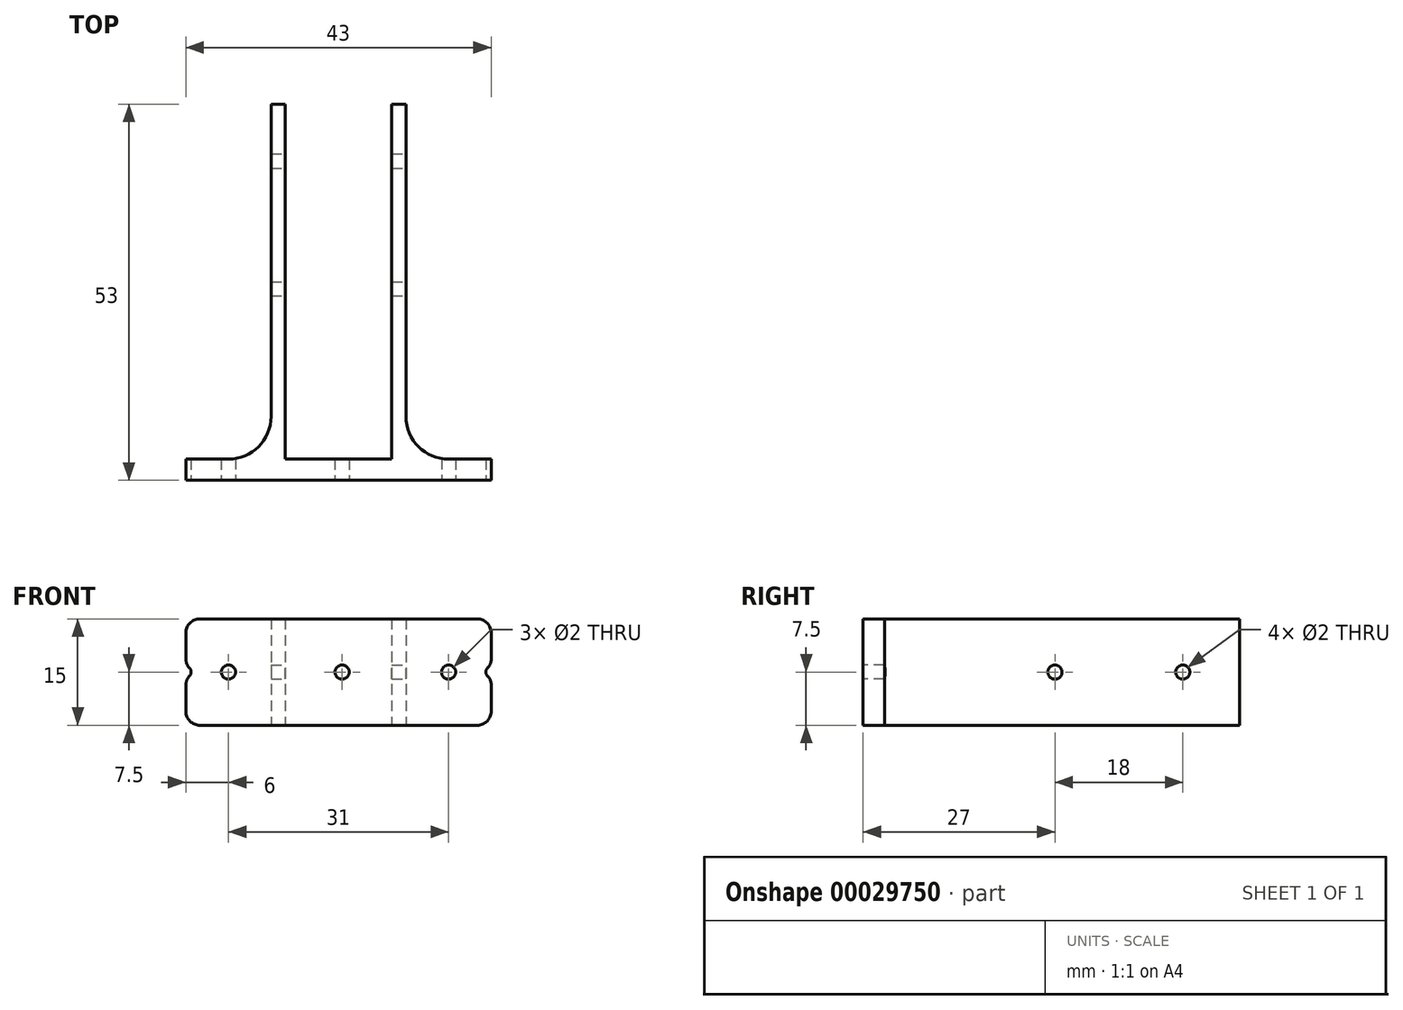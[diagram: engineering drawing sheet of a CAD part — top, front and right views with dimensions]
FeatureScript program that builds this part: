
annotation { "Feature Type Name" : "Feature", "Feature Type Description" : "" }
export const myFeature = defineFeature(function(context is Context, id is Id, definition is map)
    precondition{}
    {
        {
            var Q0;
            Q0=qCreatedBy(makeId("Top.planeOp"),FACE);
            var sketch = newSketch(context, id + "F0", { "sketchPlane" : qUnion([Q0])});
            skLineSegment(sketch, "E0.top", {"start": v(0, 53) * mm, "end": v(-2, 53) * mm});
            skLineSegment(sketch, "E0.left", {"start": v(0, 3) * mm, "end": v(0, 53) * mm});
            skLineSegment(sketch, "E0.right", {"start": v(-19, 3) * mm, "end": v(-19, 53) * mm});
            skLineSegment(sketch, "E1.top", {"start": v(-17, 3) * mm, "end": v(-2, 3) * mm});
            skLineSegment(sketch, "E1.left", {"start": v(-17, 53) * mm, "end": v(-17, 3) * mm});
            skLineSegment(sketch, "E1.right", {"start": v(-2, 53) * mm, "end": v(-2, 3) * mm});
            skLineSegment(sketch, "E2.trimOffspring", {"start": v(-17, 53) * mm, "end": v(-19, 53) * mm});
            skLineSegment(sketch, "E3", {"start": v(-19, 0) * mm, "end": v(0, 0) * mm});
            skLineSegment(sketch, "E4", {"start": v(-19, 0) * mm, "end": v(-31, 0) * mm});
            skLineSegment(sketch, "E5", {"start": v(-31, 0) * mm, "end": v(-31, 3) * mm});
            skLineSegment(sketch, "E6", {"start": v(-31, 3) * mm, "end": v(-19, 3) * mm});
            skLineSegment(sketch, "E7", {"start": v(0, 3) * mm, "end": v(12, 3) * mm});
            skLineSegment(sketch, "E8", {"start": v(12, 3) * mm, "end": v(12, 0) * mm});
            skLineSegment(sketch, "E9", {"start": v(12, 0) * mm, "end": v(0, 0) * mm});
            skSolve(sketch);
        }
        {
            var Q0;
            Q0=makeQuery(id+"F0.imprint","IMPRINT",FACE,{"disambiguationData":[TD([[makeQuery(id+"F0.imprint","IMPRINT",EDGE,{"derivedFrom":sQuery(id+"F0.wireOp",EDGE,"E0.top")}),1.0]])]});
            extrude(context, id + "F1", {"entities" : qUnion([Q0]), "depth" : 15 * mm});
        }
        {
            var Q0;
            Q0=makeQuery(id+"F1.opExtrude","SWEPT_FACE",FACE,{"disambiguationData":[OSD([sQuery(id+"F0.wireOp",EDGE,"E0.left")])]});
            var sketch = newSketch(context, id + "F2", { "sketchPlane" : qUnion([Q0])});
            skCircle(sketch, "E10", {"center": v(27, 7.5) * mm, "radius": 1 * mm});
            skCircle(sketch, "E11", {"center": v(45, 7.5) * mm, "radius": 1 * mm});
            skSolve(sketch);
        }
        {
            var Q0;
            Q0=qSketchRegion(id+"F2",true);
            extrude(context, id + "F3", {"entities" : qUnion([Q0]), "operationType" : NewBodyOperationType.REMOVE, "oppositeDirection" : true, "depth" : 25 * mm});
        }
        {
            var Q0;
            Q0=makeQuery(id+"F1.opExtrude","SWEPT_EDGE",EDGE,{"disambiguationData":[OSD([sQuery(id+"F0.wireOp",EDGE,"E0.left"),sQuery(id+"F0.wireOp",EDGE,"E7")])]});
            var Q1;
            Q1=makeQuery(id+"F1.opExtrude","SWEPT_EDGE",EDGE,{"disambiguationData":[OSD([sQuery(id+"F0.wireOp",EDGE,"E0.right"),sQuery(id+"F0.wireOp",EDGE,"E6")])]});
            fillet(context, id + "F4", {"entities" : qUnion([Q0, Q1]), "radius" : 6 * mm, "tangentPropagation" : true, "allowEdgeOverflow" : false});
        }
        {
            var Q0;
            Q0=makeQuery(id+"F1.opExtrude","SWEPT_FACE",FACE,{"disambiguationData":[OSD([sQuery(id+"F0.wireOp",EDGE,"E3"),sQuery(id+"F0.wireOp",EDGE,"E4"),sQuery(id+"F0.wireOp",EDGE,"E9")])]});
            var sketch = newSketch(context, id + "F5", { "sketchPlane" : qUnion([Q0])});
            skCircle(sketch, "E12", {"center": v(-9, 7.5) * mm, "radius": 1 * mm});
            skCircle(sketch, "E13", {"center": v(-25, 7.5) * mm, "radius": 1 * mm});
            skCircle(sketch, "E14", {"center": v(6, 7.5) * mm, "radius": 1 * mm});
            skLineSegment(sketch, "E15.0", {"start": v(12, 15) * mm, "end": v(12, 0) * mm});
            skCircle(sketch, "E16", {"center": v(-31, 7.5) * mm, "radius": 0.75 * mm});
            skCircle(sketch, "E17", {"center": v(12, 7.5) * mm, "radius": 0.75 * mm});
            skSolve(sketch);
        }
        {
            var Q0;
            Q0 = qSketchRegion(id + "F5", true);
            extrude(context, id + "F6", {"entities" : qUnion([Q0]), "operationType" : NewBodyOperationType.REMOVE, "oppositeDirection" : true, "depth" : 25 * mm});
        }
        {
            var Q0;
            Q0=makeQuery(id+"F6.boolean.opBoolean","INTERSECT",EDGE,{"disambiguationData":[OD(1.0)],"derivedFrom":[makeQuery(id+"F1.opExtrude","SWEPT_FACE",FACE,{"disambiguationData":[OSD([sQuery(id+"F0.wireOp",EDGE,"E5")])]}),makeQuery(id+"F6.opExtrude","SWEPT_FACE",FACE,{"disambiguationData":[OSD([sQuery(id+"F5.wireOp",EDGE,"E16")])]})]});
            var Q1;
            Q1=makeQuery(id+"F6.boolean.opBoolean","INTERSECT",EDGE,{"disambiguationData":[OD(0.0)],"derivedFrom":[makeQuery(id+"F1.opExtrude","SWEPT_FACE",FACE,{"disambiguationData":[OSD([sQuery(id+"F0.wireOp",EDGE,"E5")])]}),makeQuery(id+"F6.opExtrude","SWEPT_FACE",FACE,{"disambiguationData":[OSD([sQuery(id+"F5.wireOp",EDGE,"E16")])]})]});
            var Q2;
            Q2=makeQuery(id+"F6.boolean.opBoolean","INTERSECT",EDGE,{"disambiguationData":[OD(1.0)],"derivedFrom":[makeQuery(id+"F1.opExtrude","SWEPT_FACE",FACE,{"disambiguationData":[OSD([sQuery(id+"F0.wireOp",EDGE,"E8")])]}),makeQuery(id+"F6.opExtrude","SWEPT_FACE",FACE,{"disambiguationData":[OSD([sQuery(id+"F5.wireOp",EDGE,"E17")])]})]});
            var Q3;
            Q3=makeQuery(id+"F6.boolean.opBoolean","INTERSECT",EDGE,{"disambiguationData":[OD(0.0)],"derivedFrom":[makeQuery(id+"F1.opExtrude","SWEPT_FACE",FACE,{"disambiguationData":[OSD([sQuery(id+"F0.wireOp",EDGE,"E8")])]}),makeQuery(id+"F6.opExtrude","SWEPT_FACE",FACE,{"disambiguationData":[OSD([sQuery(id+"F5.wireOp",EDGE,"E17")])]})]});
            var Q4;
            Q4=makeQuery(id+"F1.opExtrude","CAP_EDGE",EDGE,{"disambiguationData":[OSD([sQuery(id+"F0.wireOp",EDGE,"E5")])],"isStart":false});
            var Q5;
            Q5=makeQuery(id+"F1.opExtrude","CAP_EDGE",EDGE,{"disambiguationData":[OSD([sQuery(id+"F0.wireOp",EDGE,"E5")])],"isStart":true});
            var Q6;
            Q6=makeQuery(id+"F1.opExtrude","CAP_EDGE",EDGE,{"disambiguationData":[OSD([sQuery(id+"F0.wireOp",EDGE,"E8")])],"isStart":false});
            var Q7;
            Q7=makeQuery(id+"F1.opExtrude","CAP_EDGE",EDGE,{"disambiguationData":[OSD([sQuery(id+"F0.wireOp",EDGE,"E8")])],"isStart":true});
            fillet(context, id + "F7", {"entities" : qUnion([Q0, Q1, Q2, Q3, Q4, Q5, Q6, Q7]), "radius" : 2 * mm, "tangentPropagation" : true, "allowEdgeOverflow" : false});
        }
    });
